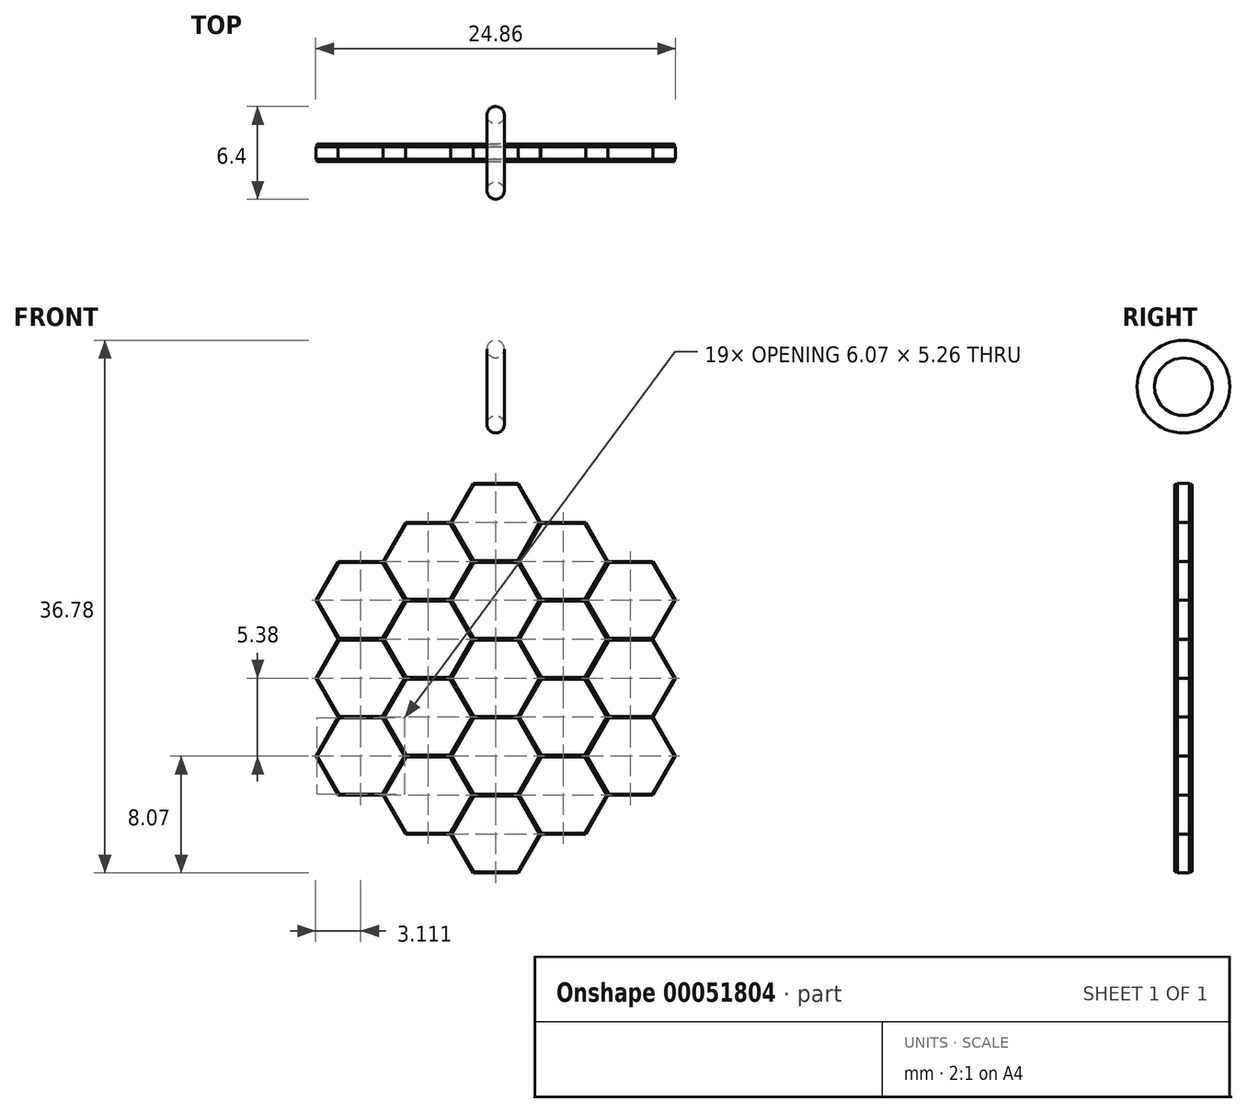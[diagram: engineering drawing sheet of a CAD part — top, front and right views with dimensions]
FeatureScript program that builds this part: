
annotation { "Feature Type Name" : "Feature", "Feature Type Description" : "" }
export const myFeature = defineFeature(function(context is Context, id is Id, definition is map)
    precondition{}
    {
        {
            var Q0;
            Q0=qCreatedBy(makeId("Front.planeOp"),FACE);
            var sketch = newSketch(context, id + "F0", { "sketchPlane" : qUnion([Q0])});
            skCircle(sketch, "E0.cCircle", {"center": v(0, 0) * mm, "radius": 4.38 * mm, "construction": true});
            skLineSegment(sketch, "E0.0", {"start": v(2.19, 3.79) * mm, "end": v(4.38, 0) * mm});
            skLineSegment(sketch, "E0.1", {"start": v(4.38, 0) * mm, "end": v(2.19, -3.79) * mm});
            skLineSegment(sketch, "E0.2", {"start": v(2.19, -3.79) * mm, "end": v(-2.19, -3.79) * mm});
            skLineSegment(sketch, "E0.3", {"start": v(-2.19, -3.79) * mm, "end": v(-4.38, 0) * mm});
            skLineSegment(sketch, "E0.4", {"start": v(-4.38, 0) * mm, "end": v(-2.19, 3.79) * mm});
            skLineSegment(sketch, "E0.5", {"start": v(-2.19, 3.79) * mm, "end": v(2.19, 3.79) * mm});
            skLineSegment(sketch, "E1.MirrorCS", {"start": v(-4.38, 7.58) * mm, "end": v(-2.19, 3.79) * mm});
            skLineSegment(sketch, "E2.MirrorCS", {"start": v(-2.19, 11.37) * mm, "end": v(-4.38, 7.58) * mm});
            skLineSegment(sketch, "E3.MirrorCS", {"start": v(2.19, 11.37) * mm, "end": v(-2.19, 11.37) * mm});
            skLineSegment(sketch, "E4.MirrorCS", {"start": v(4.38, 7.58) * mm, "end": v(2.19, 11.37) * mm});
            skLineSegment(sketch, "E5.MirrorCS", {"start": v(2.19, 3.79) * mm, "end": v(4.38, 7.58) * mm});
            skCircle(sketch, "E6.cCircle", {"center": v(0, 0) * mm, "radius": 4.28 * mm, "construction": true});
            skLineSegment(sketch, "E6.0", {"start": v(2.14, 3.7) * mm, "end": v(4.27, 0) * mm});
            skLineSegment(sketch, "E6.1", {"start": v(4.27, 0) * mm, "end": v(2.14, -3.7) * mm});
            skLineSegment(sketch, "E6.2", {"start": v(2.14, -3.7) * mm, "end": v(-2.14, -3.7) * mm});
            skLineSegment(sketch, "E6.3", {"start": v(-2.14, -3.7) * mm, "end": v(-4.27, 0) * mm});
            skLineSegment(sketch, "E6.4", {"start": v(-4.27, 0) * mm, "end": v(-2.14, 3.7) * mm});
            skLineSegment(sketch, "E6.5", {"start": v(-2.14, 3.7) * mm, "end": v(2.14, 3.7) * mm});
            skLineSegment(sketch, "E7.MirrorCS", {"start": v(-2.14, 3.88) * mm, "end": v(2.14, 3.88) * mm});
            skLineSegment(sketch, "E8.MirrorCS", {"start": v(-4.27, 7.58) * mm, "end": v(-2.14, 3.88) * mm});
            skLineSegment(sketch, "E9.MirrorCS", {"start": v(-2.14, 11.28) * mm, "end": v(-4.27, 7.58) * mm});
            skLineSegment(sketch, "E10.MirrorCS", {"start": v(2.14, 11.28) * mm, "end": v(-2.14, 11.28) * mm});
            skLineSegment(sketch, "E11.MirrorCS", {"start": v(4.27, 7.58) * mm, "end": v(2.14, 11.28) * mm});
            skLineSegment(sketch, "E12.MirrorCS", {"start": v(2.14, 3.88) * mm, "end": v(4.27, 7.58) * mm});
            skLineSegment(sketch, "E13.MirrorCS", {"start": v(2.29, 3.79) * mm, "end": v(4.43, 0.09) * mm});
            skLineSegment(sketch, "E14.MirrorCS", {"start": v(4.43, 7.5) * mm, "end": v(2.29, 3.79) * mm});
            skLineSegment(sketch, "E15.MirrorCS", {"start": v(8.7, 7.5) * mm, "end": v(4.42, 7.5) * mm});
            skLineSegment(sketch, "E16.MirrorCS", {"start": v(8.75, 7.58) * mm, "end": v(4.38, 7.58) * mm});
            skLineSegment(sketch, "E17.MirrorCS", {"start": v(10.84, 3.79) * mm, "end": v(8.7, 7.5) * mm});
            skLineSegment(sketch, "E18.MirrorCS", {"start": v(10.94, 3.79) * mm, "end": v(8.75, 7.58) * mm});
            skLineSegment(sketch, "E19.MirrorCS", {"start": v(8.7, 0.09) * mm, "end": v(10.84, 3.79) * mm});
            skLineSegment(sketch, "E20.MirrorCS", {"start": v(8.75, 0) * mm, "end": v(10.94, 3.79) * mm});
            skLineSegment(sketch, "E21.MirrorCS", {"start": v(4.43, 0.09) * mm, "end": v(8.7, 0.09) * mm});
            skLineSegment(sketch, "E22.MirrorCS", {"start": v(4.38, 0) * mm, "end": v(8.75, 0) * mm});
            skLineSegment(sketch, "E23.MirrorCS", {"start": v(4.43, -0.09) * mm, "end": v(2.29, -3.79) * mm});
            skLineSegment(sketch, "E24.MirrorCS", {"start": v(8.7, -0.09) * mm, "end": v(4.43, -0.09) * mm});
            skLineSegment(sketch, "E25.MirrorCS", {"start": v(10.84, -3.79) * mm, "end": v(8.7, -0.09) * mm});
            skLineSegment(sketch, "E26.MirrorCS", {"start": v(10.94, -3.79) * mm, "end": v(8.75, 0) * mm});
            skLineSegment(sketch, "E27.MirrorCS", {"start": v(8.7, -7.5) * mm, "end": v(10.84, -3.79) * mm});
            skLineSegment(sketch, "E28.MirrorCS", {"start": v(8.75, -7.58) * mm, "end": v(10.94, -3.79) * mm});
            skLineSegment(sketch, "E29.MirrorCS", {"start": v(4.43, -7.5) * mm, "end": v(8.7, -7.5) * mm});
            skLineSegment(sketch, "E30.MirrorCS", {"start": v(4.38, -7.58) * mm, "end": v(8.75, -7.58) * mm});
            skLineSegment(sketch, "E31.MirrorCS", {"start": v(2.29, -3.79) * mm, "end": v(4.43, -7.5) * mm});
            skLineSegment(sketch, "E32.MirrorCS", {"start": v(2.19, -3.79) * mm, "end": v(4.38, -7.58) * mm});
            skLineSegment(sketch, "E33.MirrorCS", {"start": v(2.14, -3.88) * mm, "end": v(-2.14, -3.88) * mm});
            skLineSegment(sketch, "E34.MirrorCS", {"start": v(4.27, -7.58) * mm, "end": v(2.14, -3.88) * mm});
            skLineSegment(sketch, "E35.MirrorCS", {"start": v(2.14, -11.28) * mm, "end": v(4.27, -7.58) * mm});
            skLineSegment(sketch, "E36.MirrorCS", {"start": v(2.19, -11.37) * mm, "end": v(4.38, -7.58) * mm});
            skLineSegment(sketch, "E37.MirrorCS", {"start": v(-2.14, -11.28) * mm, "end": v(2.14, -11.28) * mm});
            skLineSegment(sketch, "E38.MirrorCS", {"start": v(-2.19, -11.37) * mm, "end": v(2.19, -11.37) * mm});
            skLineSegment(sketch, "E39.MirrorCS", {"start": v(-4.27, -7.58) * mm, "end": v(-2.14, -11.28) * mm});
            skLineSegment(sketch, "E40.MirrorCS", {"start": v(-4.38, -7.58) * mm, "end": v(-2.19, -11.37) * mm});
            skLineSegment(sketch, "E41.MirrorCS", {"start": v(-2.14, -3.88) * mm, "end": v(-4.27, -7.58) * mm});
            skLineSegment(sketch, "E42.MirrorCS", {"start": v(-2.19, -3.79) * mm, "end": v(-4.38, -7.58) * mm});
            skLineSegment(sketch, "E43.MirrorCS", {"start": v(-2.29, -3.79) * mm, "end": v(-4.43, -0.09) * mm});
            skLineSegment(sketch, "E44.MirrorCS", {"start": v(-4.43, -0.09) * mm, "end": v(-8.7, -0.09) * mm});
            skLineSegment(sketch, "E45.MirrorCS", {"start": v(-4.38, 0) * mm, "end": v(-8.75, 0) * mm});
            skLineSegment(sketch, "E46.MirrorCS", {"start": v(-8.7, -0.09) * mm, "end": v(-10.84, -3.79) * mm});
            skLineSegment(sketch, "E47.MirrorCS", {"start": v(-8.75, 0) * mm, "end": v(-10.94, -3.79) * mm});
            skLineSegment(sketch, "E48.MirrorCS", {"start": v(-10.84, -3.79) * mm, "end": v(-8.7, -7.5) * mm});
            skLineSegment(sketch, "E49.MirrorCS", {"start": v(-10.94, -3.79) * mm, "end": v(-8.75, -7.58) * mm});
            skLineSegment(sketch, "E50.MirrorCS", {"start": v(-8.7, -7.5) * mm, "end": v(-4.42, -7.5) * mm});
            skLineSegment(sketch, "E51.MirrorCS", {"start": v(-8.75, -7.58) * mm, "end": v(-4.38, -7.58) * mm});
            skLineSegment(sketch, "E52.MirrorCS", {"start": v(-4.42, -7.5) * mm, "end": v(-2.29, -3.79) * mm});
            skLineSegment(sketch, "E53.MirrorCS", {"start": v(-4.42, 0.09) * mm, "end": v(-2.29, 3.79) * mm});
            skLineSegment(sketch, "E54.MirrorCS", {"start": v(-2.29, 3.79) * mm, "end": v(-4.43, 7.5) * mm});
            skLineSegment(sketch, "E55.MirrorCS", {"start": v(-4.42, 7.5) * mm, "end": v(-8.7, 7.5) * mm});
            skLineSegment(sketch, "E56.MirrorCS", {"start": v(-8.7, 7.5) * mm, "end": v(-10.84, 3.79) * mm});
            skLineSegment(sketch, "E57.MirrorCS", {"start": v(-10.84, 3.79) * mm, "end": v(-8.7, 0.09) * mm});
            skLineSegment(sketch, "E58.MirrorCS", {"start": v(-8.7, 0.09) * mm, "end": v(-4.42, 0.09) * mm});
            skLineSegment(sketch, "E59.MirrorCS", {"start": v(-8.75, 7.58) * mm, "end": v(-10.94, 3.79) * mm});
            skLineSegment(sketch, "E60.MirrorCS", {"start": v(-4.38, 7.58) * mm, "end": v(-8.75, 7.58) * mm});
            skLineSegment(sketch, "E61.MirrorCS", {"start": v(-10.94, 3.79) * mm, "end": v(-8.75, 0) * mm});
            skLineSegment(sketch, "E62.MirrorCS", {"start": v(10.99, 3.88) * mm, "end": v(8.85, 7.58) * mm});
            skLineSegment(sketch, "E63.MirrorCS", {"start": v(8.75, 7.58) * mm, "end": v(10.94, 11.37) * mm});
            skLineSegment(sketch, "E64.MirrorCS", {"start": v(8.85, 7.58) * mm, "end": v(10.99, 11.28) * mm});
            skLineSegment(sketch, "E65.MirrorCS", {"start": v(10.99, 11.28) * mm, "end": v(15.26, 11.28) * mm});
            skLineSegment(sketch, "E66.MirrorCS", {"start": v(15.31, 11.37) * mm, "end": v(10.94, 11.37) * mm});
            skLineSegment(sketch, "E67.MirrorCS", {"start": v(15.26, 11.28) * mm, "end": v(17.4, 7.58) * mm});
            skLineSegment(sketch, "E68.MirrorCS", {"start": v(15.31, 11.37) * mm, "end": v(17.5, 7.58) * mm});
            skLineSegment(sketch, "E69.MirrorCS", {"start": v(17.4, 7.58) * mm, "end": v(15.26, 3.88) * mm});
            skLineSegment(sketch, "E70.MirrorCS", {"start": v(17.5, 7.58) * mm, "end": v(15.31, 3.79) * mm});
            skLineSegment(sketch, "E71.MirrorCS", {"start": v(15.26, 3.88) * mm, "end": v(10.99, 3.88) * mm});
            skLineSegment(sketch, "E72.MirrorCS", {"start": v(15.31, 3.79) * mm, "end": v(10.94, 3.79) * mm});
            skLineSegment(sketch, "E73.MirrorCS", {"start": v(8.85, 0) * mm, "end": v(10.99, 3.7) * mm});
            skLineSegment(sketch, "E74.MirrorCS", {"start": v(10.99, 3.7) * mm, "end": v(15.26, 3.7) * mm});
            skLineSegment(sketch, "E75.MirrorCS", {"start": v(15.26, 3.7) * mm, "end": v(17.4, 0) * mm});
            skLineSegment(sketch, "E76.MirrorCS", {"start": v(17.4, 0) * mm, "end": v(15.26, -3.7) * mm});
            skLineSegment(sketch, "E77.MirrorCS", {"start": v(15.26, -3.7) * mm, "end": v(10.99, -3.7) * mm});
            skLineSegment(sketch, "E78.MirrorCS", {"start": v(10.99, -3.7) * mm, "end": v(8.85, 0) * mm});
            skLineSegment(sketch, "E79.MirrorCS", {"start": v(15.31, 3.79) * mm, "end": v(17.5, 0) * mm});
            skLineSegment(sketch, "E80.MirrorCS", {"start": v(15.31, -3.79) * mm, "end": v(17.5, 0) * mm});
            skLineSegment(sketch, "E81.MirrorCS", {"start": v(15.31, -3.79) * mm, "end": v(10.94, -3.79) * mm});
            skLineSegment(sketch, "E82.MirrorCS", {"start": v(2.14, 11.45) * mm, "end": v(-2.14, 11.45) * mm});
            skLineSegment(sketch, "E83.MirrorCS", {"start": v(-2.14, 11.45) * mm, "end": v(-4.27, 15.16) * mm});
            skLineSegment(sketch, "E84.MirrorCS", {"start": v(-2.19, 11.37) * mm, "end": v(-4.38, 15.16) * mm});
            skLineSegment(sketch, "E85.MirrorCS", {"start": v(-4.27, 15.16) * mm, "end": v(-2.14, 18.86) * mm});
            skLineSegment(sketch, "E86.MirrorCS", {"start": v(-4.38, 15.16) * mm, "end": v(-2.19, 18.94) * mm});
            skLineSegment(sketch, "E87.MirrorCS", {"start": v(-2.14, 18.86) * mm, "end": v(2.14, 18.86) * mm});
            skLineSegment(sketch, "E88.MirrorCS", {"start": v(-2.19, 18.94) * mm, "end": v(2.19, 18.94) * mm});
            skLineSegment(sketch, "E89.MirrorCS", {"start": v(2.14, 18.86) * mm, "end": v(4.27, 15.16) * mm});
            skLineSegment(sketch, "E90.MirrorCS", {"start": v(2.19, 18.94) * mm, "end": v(4.37, 15.16) * mm});
            skLineSegment(sketch, "E91.MirrorCS", {"start": v(4.27, 15.16) * mm, "end": v(2.14, 11.45) * mm});
            skLineSegment(sketch, "E92.MirrorCS", {"start": v(4.37, 15.16) * mm, "end": v(2.19, 11.37) * mm});
            skLineSegment(sketch, "E93.MirrorCS", {"start": v(-2.14, -11.45) * mm, "end": v(2.14, -11.45) * mm});
            skLineSegment(sketch, "E94.MirrorCS", {"start": v(-4.27, -15.16) * mm, "end": v(-2.14, -11.45) * mm});
            skLineSegment(sketch, "E95.MirrorCS", {"start": v(-4.37, -15.16) * mm, "end": v(-2.19, -11.37) * mm});
            skLineSegment(sketch, "E96.MirrorCS", {"start": v(-2.14, -18.86) * mm, "end": v(-4.27, -15.16) * mm});
            skLineSegment(sketch, "E97.MirrorCS", {"start": v(-2.19, -18.94) * mm, "end": v(-4.38, -15.16) * mm});
            skLineSegment(sketch, "E98.MirrorCS", {"start": v(2.14, -18.86) * mm, "end": v(-2.14, -18.86) * mm});
            skLineSegment(sketch, "E99.MirrorCS", {"start": v(2.19, -18.94) * mm, "end": v(-2.19, -18.94) * mm});
            skLineSegment(sketch, "E100.MirrorCS", {"start": v(4.27, -15.16) * mm, "end": v(2.14, -18.86) * mm});
            skLineSegment(sketch, "E101.MirrorCS", {"start": v(2.19, -18.94) * mm, "end": v(4.38, -15.16) * mm});
            skLineSegment(sketch, "E102.MirrorCS", {"start": v(2.14, -11.45) * mm, "end": v(4.27, -15.16) * mm});
            skLineSegment(sketch, "E103.MirrorCS", {"start": v(2.19, -11.37) * mm, "end": v(4.38, -15.16) * mm});
            skLineSegment(sketch, "E104.MirrorCS", {"start": v(8.7, 7.66) * mm, "end": v(4.42, 7.66) * mm});
            skLineSegment(sketch, "E105.MirrorCS", {"start": v(4.43, 7.66) * mm, "end": v(2.29, 11.37) * mm});
            skLineSegment(sketch, "E106.MirrorCS", {"start": v(2.29, 11.37) * mm, "end": v(4.42, 15.07) * mm});
            skLineSegment(sketch, "E107.MirrorCS", {"start": v(4.42, 15.07) * mm, "end": v(8.7, 15.07) * mm});
            skLineSegment(sketch, "E108.MirrorCS", {"start": v(8.7, 15.07) * mm, "end": v(10.84, 11.37) * mm});
            skLineSegment(sketch, "E109.MirrorCS", {"start": v(10.84, 11.37) * mm, "end": v(8.7, 7.66) * mm});
            skLineSegment(sketch, "E110.MirrorCS", {"start": v(8.75, 15.16) * mm, "end": v(10.94, 11.37) * mm});
            skLineSegment(sketch, "E111.MirrorCS", {"start": v(4.37, 15.16) * mm, "end": v(8.75, 15.16) * mm});
            skLineSegment(sketch, "E112.MirrorCS", {"start": v(4.43, -7.66) * mm, "end": v(8.7, -7.66) * mm});
            skLineSegment(sketch, "E113.MirrorCS", {"start": v(2.29, -11.37) * mm, "end": v(4.43, -7.66) * mm});
            skLineSegment(sketch, "E114.MirrorCS", {"start": v(4.43, -15.07) * mm, "end": v(2.29, -11.37) * mm});
            skLineSegment(sketch, "E115.MirrorCS", {"start": v(8.7, -15.07) * mm, "end": v(4.43, -15.07) * mm});
            skLineSegment(sketch, "E116.MirrorCS", {"start": v(4.38, -15.16) * mm, "end": v(8.75, -15.16) * mm});
            skLineSegment(sketch, "E117.MirrorCS", {"start": v(10.84, -11.37) * mm, "end": v(8.7, -15.07) * mm});
            skLineSegment(sketch, "E118.MirrorCS", {"start": v(10.94, -11.37) * mm, "end": v(8.75, -15.16) * mm});
            skLineSegment(sketch, "E119.MirrorCS", {"start": v(8.7, -7.66) * mm, "end": v(10.84, -11.37) * mm});
            skLineSegment(sketch, "E120.MirrorCS", {"start": v(8.75, -7.58) * mm, "end": v(10.94, -11.37) * mm});
            skLineSegment(sketch, "E121.MirrorCS", {"start": v(8.85, -7.58) * mm, "end": v(10.99, -3.88) * mm});
            skLineSegment(sketch, "E122.MirrorCS", {"start": v(10.99, -11.28) * mm, "end": v(8.85, -7.58) * mm});
            skLineSegment(sketch, "E123.MirrorCS", {"start": v(15.26, -11.28) * mm, "end": v(10.99, -11.28) * mm});
            skLineSegment(sketch, "E124.MirrorCS", {"start": v(15.31, -11.37) * mm, "end": v(10.94, -11.37) * mm});
            skLineSegment(sketch, "E125.MirrorCS", {"start": v(17.4, -7.58) * mm, "end": v(15.26, -11.28) * mm});
            skLineSegment(sketch, "E126.MirrorCS", {"start": v(17.5, -7.58) * mm, "end": v(15.31, -11.37) * mm});
            skLineSegment(sketch, "E127.MirrorCS", {"start": v(15.26, -3.88) * mm, "end": v(17.4, -7.58) * mm});
            skLineSegment(sketch, "E128.MirrorCS", {"start": v(17.5, -7.58) * mm, "end": v(15.31, -3.79) * mm});
            skLineSegment(sketch, "E129.MirrorCS", {"start": v(10.99, -3.88) * mm, "end": v(15.26, -3.88) * mm});
            skLineSegment(sketch, "E130.MirrorCS", {"start": v(-4.42, 7.66) * mm, "end": v(-8.7, 7.66) * mm});
            skLineSegment(sketch, "E131.MirrorCS", {"start": v(-2.29, 11.37) * mm, "end": v(-4.42, 7.66) * mm});
            skLineSegment(sketch, "E132.MirrorCS", {"start": v(-4.43, 15.07) * mm, "end": v(-2.29, 11.37) * mm});
            skLineSegment(sketch, "E133.MirrorCS", {"start": v(-8.7, 15.07) * mm, "end": v(-4.42, 15.07) * mm});
            skLineSegment(sketch, "E134.MirrorCS", {"start": v(-10.84, 11.37) * mm, "end": v(-8.7, 15.07) * mm});
            skLineSegment(sketch, "E135.MirrorCS", {"start": v(-8.7, 7.66) * mm, "end": v(-10.84, 11.37) * mm});
            skLineSegment(sketch, "E136.MirrorCS", {"start": v(-8.75, 7.58) * mm, "end": v(-10.94, 11.37) * mm});
            skLineSegment(sketch, "E137.MirrorCS", {"start": v(-10.94, 11.37) * mm, "end": v(-8.75, 15.16) * mm});
            skLineSegment(sketch, "E138.MirrorCS", {"start": v(-4.38, 15.16) * mm, "end": v(-8.75, 15.16) * mm});
            skLineSegment(sketch, "E139.MirrorCS", {"start": v(-8.7, -7.66) * mm, "end": v(-4.42, -7.66) * mm});
            skLineSegment(sketch, "E140.MirrorCS", {"start": v(-4.42, -7.66) * mm, "end": v(-2.29, -11.37) * mm});
            skLineSegment(sketch, "E141.MirrorCS", {"start": v(-2.29, -11.37) * mm, "end": v(-4.42, -15.07) * mm});
            skLineSegment(sketch, "E142.MirrorCS", {"start": v(-4.42, -15.07) * mm, "end": v(-8.7, -15.07) * mm});
            skLineSegment(sketch, "E143.MirrorCS", {"start": v(-4.37, -15.16) * mm, "end": v(-8.75, -15.16) * mm});
            skLineSegment(sketch, "E144.MirrorCS", {"start": v(-8.7, -15.07) * mm, "end": v(-10.84, -11.37) * mm});
            skLineSegment(sketch, "E145.MirrorCS", {"start": v(-8.75, -15.16) * mm, "end": v(-10.94, -11.37) * mm});
            skLineSegment(sketch, "E146.MirrorCS", {"start": v(-10.84, -11.37) * mm, "end": v(-8.7, -7.66) * mm});
            skLineSegment(sketch, "E147.MirrorCS", {"start": v(-10.94, -11.37) * mm, "end": v(-8.75, -7.58) * mm});
            skLineSegment(sketch, "E148.MirrorCS", {"start": v(-8.85, 7.58) * mm, "end": v(-10.99, 11.28) * mm});
            skLineSegment(sketch, "E149.MirrorCS", {"start": v(-10.99, 11.28) * mm, "end": v(-15.26, 11.28) * mm});
            skLineSegment(sketch, "E150.MirrorCS", {"start": v(-15.26, 11.28) * mm, "end": v(-17.4, 7.58) * mm});
            skLineSegment(sketch, "E151.MirrorCS", {"start": v(-17.4, 7.58) * mm, "end": v(-15.26, 3.88) * mm});
            skLineSegment(sketch, "E152.MirrorCS", {"start": v(-15.26, 3.88) * mm, "end": v(-10.99, 3.88) * mm});
            skLineSegment(sketch, "E153.MirrorCS", {"start": v(-10.99, 3.88) * mm, "end": v(-8.85, 7.58) * mm});
            skLineSegment(sketch, "E154.MirrorCS", {"start": v(-10.94, 11.37) * mm, "end": v(-15.31, 11.37) * mm});
            skLineSegment(sketch, "E155.MirrorCS", {"start": v(-17.5, 7.58) * mm, "end": v(-15.31, 11.37) * mm});
            skLineSegment(sketch, "E156.MirrorCS", {"start": v(-15.31, 3.79) * mm, "end": v(-17.5, 7.58) * mm});
            skLineSegment(sketch, "E157.MirrorCS", {"start": v(-15.31, 3.79) * mm, "end": v(-10.94, 3.79) * mm});
            skLineSegment(sketch, "E158.MirrorCS", {"start": v(-15.26, 3.7) * mm, "end": v(-10.99, 3.7) * mm});
            skLineSegment(sketch, "E159.MirrorCS", {"start": v(-17.4, 0) * mm, "end": v(-15.26, 3.7) * mm});
            skLineSegment(sketch, "E160.MirrorCS", {"start": v(-15.26, -3.7) * mm, "end": v(-17.4, 0) * mm});
            skLineSegment(sketch, "E161.MirrorCS", {"start": v(-15.31, 3.79) * mm, "end": v(-17.5, 0) * mm});
            skLineSegment(sketch, "E162.MirrorCS", {"start": v(-17.5, 0) * mm, "end": v(-15.31, -3.79) * mm});
            skLineSegment(sketch, "E163.MirrorCS", {"start": v(-10.99, -3.7) * mm, "end": v(-15.26, -3.7) * mm});
            skLineSegment(sketch, "E164.MirrorCS", {"start": v(-10.94, -3.79) * mm, "end": v(-15.31, -3.79) * mm});
            skLineSegment(sketch, "E165.MirrorCS", {"start": v(-8.85, 0) * mm, "end": v(-10.99, -3.7) * mm});
            skLineSegment(sketch, "E166.MirrorCS", {"start": v(-10.99, 3.7) * mm, "end": v(-8.85, 0) * mm});
            skLineSegment(sketch, "E167.MirrorCS", {"start": v(-10.99, -3.88) * mm, "end": v(-15.26, -3.88) * mm});
            skLineSegment(sketch, "E168.MirrorCS", {"start": v(-15.26, -3.88) * mm, "end": v(-17.4, -7.58) * mm});
            skLineSegment(sketch, "E169.MirrorCS", {"start": v(-17.5, -7.58) * mm, "end": v(-15.31, -3.79) * mm});
            skLineSegment(sketch, "E170.MirrorCS", {"start": v(-17.4, -7.58) * mm, "end": v(-15.26, -11.28) * mm});
            skLineSegment(sketch, "E171.MirrorCS", {"start": v(-15.31, -11.37) * mm, "end": v(-17.5, -7.58) * mm});
            skLineSegment(sketch, "E172.MirrorCS", {"start": v(-15.26, -11.28) * mm, "end": v(-10.99, -11.28) * mm});
            skLineSegment(sketch, "E173.MirrorCS", {"start": v(-15.31, -11.37) * mm, "end": v(-10.94, -11.37) * mm});
            skLineSegment(sketch, "E174.MirrorCS", {"start": v(-10.99, -11.28) * mm, "end": v(-8.85, -7.58) * mm});
            skLineSegment(sketch, "E175.MirrorCS", {"start": v(-8.85, -7.58) * mm, "end": v(-10.99, -3.88) * mm});
            skSolve(sketch);
        }
        {
            var Q0;
            Q0=makeQuery(id+"F0.imprint","IMPRINT",FACE,{"disambiguationData":[TD([[makeQuery(id+"F0.imprint","IMPRINT",EDGE,{"derivedFrom":sQuery(id+"F0.wireOp",EDGE,"E0.3")}),1.0]])]});
            var Q1;
            Q1=makeQuery(id+"F0.imprint","IMPRINT",FACE,{"disambiguationData":[TD([[makeQuery(id+"F0.imprint","IMPRINT",EDGE,{"derivedFrom":sQuery(id+"F0.wireOp",EDGE,"E47.MirrorCS")}),-1.0]])]});
            var Q2;
            Q2=makeQuery(id+"F0.imprint","IMPRINT",FACE,{"disambiguationData":[TD([[makeQuery(id+"F0.imprint","IMPRINT",EDGE,{"derivedFrom":sQuery(id+"F0.wireOp",EDGE,"E49.MirrorCS")}),-1.0]])]});
            var Q3;
            Q3=makeQuery(id+"F0.imprint","IMPRINT",FACE,{"disambiguationData":[TD([[makeQuery(id+"F0.imprint","IMPRINT",EDGE,{"derivedFrom":sQuery(id+"F0.wireOp",EDGE,"E0.4")}),1.0]])]});
            var Q4;
            Q4=makeQuery(id+"F0.imprint","IMPRINT",FACE,{"disambiguationData":[TD([[makeQuery(id+"F0.imprint","IMPRINT",EDGE,{"derivedFrom":sQuery(id+"F0.wireOp",EDGE,"E59.MirrorCS")}),-1.0]])]});
            var Q5;
            Q5=makeQuery(id+"F0.imprint","IMPRINT",FACE,{"disambiguationData":[TD([[makeQuery(id+"F0.imprint","IMPRINT",EDGE,{"derivedFrom":sQuery(id+"F0.wireOp",EDGE,"E0.0")}),-1.0]])]});
            var Q6;
            Q6=makeQuery(id+"F0.imprint","IMPRINT",FACE,{"disambiguationData":[TD([[makeQuery(id+"F0.imprint","IMPRINT",EDGE,{"derivedFrom":sQuery(id+"F0.wireOp",EDGE,"E0.2")}),1.0]])]});
            var Q7;
            Q7=makeQuery(id+"F0.imprint","IMPRINT",FACE,{"disambiguationData":[TD([[makeQuery(id+"F0.imprint","IMPRINT",EDGE,{"derivedFrom":sQuery(id+"F0.wireOp",EDGE,"E40.MirrorCS")}),-1.0]])]});
            var Q8;
            Q8=makeQuery(id+"F0.imprint","IMPRINT",FACE,{"disambiguationData":[TD([[makeQuery(id+"F0.imprint","IMPRINT",EDGE,{"derivedFrom":sQuery(id+"F0.wireOp",EDGE,"E38.MirrorCS")}),-1.0]])]});
            var Q9;
            Q9=makeQuery(id+"F0.imprint","IMPRINT",FACE,{"disambiguationData":[TD([[makeQuery(id+"F0.imprint","IMPRINT",EDGE,{"derivedFrom":sQuery(id+"F0.wireOp",EDGE,"E30.MirrorCS")}),-1.0]])]});
            var Q10;
            Q10=makeQuery(id+"F0.imprint","IMPRINT",FACE,{"disambiguationData":[TD([[makeQuery(id+"F0.imprint","IMPRINT",EDGE,{"derivedFrom":sQuery(id+"F0.wireOp",EDGE,"E0.1")}),1.0]])]});
            var Q11;
            Q11=makeQuery(id+"F0.imprint","IMPRINT",FACE,{"disambiguationData":[TD([[makeQuery(id+"F0.imprint","IMPRINT",EDGE,{"derivedFrom":sQuery(id+"F0.wireOp",EDGE,"E0.0")}),1.0]])]});
            var Q12;
            Q12=makeQuery(id+"F0.imprint","IMPRINT",FACE,{"disambiguationData":[TD([[makeQuery(id+"F0.imprint","IMPRINT",EDGE,{"derivedFrom":sQuery(id+"F0.wireOp",EDGE,"E0.5")}),1.0]])]});
            var Q13;
            Q13=makeQuery(id+"F0.imprint","IMPRINT",FACE,{"disambiguationData":[TD([[makeQuery(id+"F0.imprint","IMPRINT",EDGE,{"derivedFrom":sQuery(id+"F0.wireOp",EDGE,"E2.MirrorCS")}),-1.0]])]});
            var Q14;
            Q14=makeQuery(id+"F0.imprint","IMPRINT",FACE,{"disambiguationData":[TD([[makeQuery(id+"F0.imprint","IMPRINT",EDGE,{"derivedFrom":sQuery(id+"F0.wireOp",EDGE,"E3.MirrorCS")}),-1.0]])]});
            var Q15;
            Q15=makeQuery(id+"F0.imprint","IMPRINT",FACE,{"disambiguationData":[TD([[makeQuery(id+"F0.imprint","IMPRINT",EDGE,{"derivedFrom":sQuery(id+"F0.wireOp",EDGE,"E4.MirrorCS")}),-1.0]])]});
            var Q16;
            Q16=makeQuery(id+"F0.imprint","IMPRINT",FACE,{"disambiguationData":[TD([[makeQuery(id+"F0.imprint","IMPRINT",EDGE,{"derivedFrom":sQuery(id+"F0.wireOp",EDGE,"E18.MirrorCS")}),-1.0]])]});
            var Q17;
            Q17=makeQuery(id+"F0.imprint","IMPRINT",FACE,{"disambiguationData":[TD([[makeQuery(id+"F0.imprint","IMPRINT",EDGE,{"derivedFrom":sQuery(id+"F0.wireOp",EDGE,"E20.MirrorCS")}),-1.0]])]});
            var Q18;
            Q18=makeQuery(id+"F0.imprint","IMPRINT",FACE,{"disambiguationData":[TD([[makeQuery(id+"F0.imprint","IMPRINT",EDGE,{"derivedFrom":sQuery(id+"F0.wireOp",EDGE,"E28.MirrorCS")}),-1.0]])]});
            extrude(context, id + "F1", {"entities" : qUnion([Q0, Q1, Q2, Q3, Q4, Q5, Q6, Q7, Q8, Q9, Q10, Q11, Q12, Q13, Q14, Q15, Q16, Q17, Q18]), "endBound" : BoundingType.SYMMETRIC, "offsetDistance" : 25 * mm, "depth" : 1.2 * mm});
        }
        {
            var Q0;
            Q0=makeQuery(id+"F0.imprint","IMPRINT",FACE,{"disambiguationData":[TD([[makeQuery(id+"F0.imprint","IMPRINT",EDGE,{"derivedFrom":sQuery(id+"F0.wireOp",EDGE,"E167.MirrorCS")}),1.0]])]});
            var Q1;
            Q1=makeQuery(id+"F0.imprint","IMPRINT",FACE,{"disambiguationData":[TD([[makeQuery(id+"F0.imprint","IMPRINT",EDGE,{"derivedFrom":sQuery(id+"F0.wireOp",EDGE,"E158.MirrorCS")}),-1.0]])]});
            var Q2;
            Q2=makeQuery(id+"F0.imprint","IMPRINT",FACE,{"disambiguationData":[TD([[makeQuery(id+"F0.imprint","IMPRINT",EDGE,{"derivedFrom":sQuery(id+"F0.wireOp",EDGE,"E148.MirrorCS")}),1.0]])]});
            var Q3;
            Q3=makeQuery(id+"F0.imprint","IMPRINT",FACE,{"disambiguationData":[TD([[makeQuery(id+"F0.imprint","IMPRINT",EDGE,{"derivedFrom":sQuery(id+"F0.wireOp",EDGE,"E139.MirrorCS")}),-1.0]])]});
            var Q4;
            Q4=makeQuery(id+"F0.imprint","IMPRINT",FACE,{"disambiguationData":[TD([[makeQuery(id+"F0.imprint","IMPRINT",EDGE,{"derivedFrom":sQuery(id+"F0.wireOp",EDGE,"E43.MirrorCS")}),1.0]])]});
            var Q5;
            Q5=makeQuery(id+"F0.imprint","IMPRINT",FACE,{"disambiguationData":[TD([[makeQuery(id+"F0.imprint","IMPRINT",EDGE,{"derivedFrom":sQuery(id+"F0.wireOp",EDGE,"E53.MirrorCS")}),1.0]])]});
            var Q6;
            Q6=makeQuery(id+"F0.imprint","IMPRINT",FACE,{"disambiguationData":[TD([[makeQuery(id+"F0.imprint","IMPRINT",EDGE,{"derivedFrom":sQuery(id+"F0.wireOp",EDGE,"E130.MirrorCS")}),-1.0]])]});
            var Q7;
            Q7=makeQuery(id+"F0.imprint","IMPRINT",FACE,{"disambiguationData":[TD([[makeQuery(id+"F0.imprint","IMPRINT",EDGE,{"derivedFrom":sQuery(id+"F0.wireOp",EDGE,"E93.MirrorCS")}),-1.0]])]});
            var Q8;
            Q8=makeQuery(id+"F0.imprint","IMPRINT",FACE,{"disambiguationData":[TD([[makeQuery(id+"F0.imprint","IMPRINT",EDGE,{"derivedFrom":sQuery(id+"F0.wireOp",EDGE,"E33.MirrorCS")}),1.0]])]});
            var Q9;
            Q9=makeQuery(id+"F0.imprint","IMPRINT",FACE,{"disambiguationData":[TD([[makeQuery(id+"F0.imprint","IMPRINT",EDGE,{"derivedFrom":sQuery(id+"F0.wireOp",EDGE,"E7.MirrorCS")}),1.0]])]});
            var Q10;
            Q10=makeQuery(id+"F0.imprint","IMPRINT",FACE,{"disambiguationData":[TD([[makeQuery(id+"F0.imprint","IMPRINT",EDGE,{"derivedFrom":sQuery(id+"F0.wireOp",EDGE,"E82.MirrorCS")}),-1.0]])]});
            var Q11;
            Q11=makeQuery(id+"F0.imprint","IMPRINT",FACE,{"disambiguationData":[TD([[makeQuery(id+"F0.imprint","IMPRINT",EDGE,{"derivedFrom":sQuery(id+"F0.wireOp",EDGE,"E112.MirrorCS")}),-1.0]])]});
            var Q12;
            Q12=makeQuery(id+"F0.imprint","IMPRINT",FACE,{"disambiguationData":[TD([[makeQuery(id+"F0.imprint","IMPRINT",EDGE,{"derivedFrom":sQuery(id+"F0.wireOp",EDGE,"E23.MirrorCS")}),1.0]])]});
            var Q13;
            Q13=makeQuery(id+"F0.imprint","IMPRINT",FACE,{"disambiguationData":[TD([[makeQuery(id+"F0.imprint","IMPRINT",EDGE,{"derivedFrom":sQuery(id+"F0.wireOp",EDGE,"E13.MirrorCS")}),1.0]])]});
            var Q14;
            Q14=makeQuery(id+"F0.imprint","IMPRINT",FACE,{"disambiguationData":[TD([[makeQuery(id+"F0.imprint","IMPRINT",EDGE,{"derivedFrom":sQuery(id+"F0.wireOp",EDGE,"E104.MirrorCS")}),-1.0]])]});
            var Q15;
            Q15=makeQuery(id+"F0.imprint","IMPRINT",FACE,{"disambiguationData":[TD([[makeQuery(id+"F0.imprint","IMPRINT",EDGE,{"derivedFrom":sQuery(id+"F0.wireOp",EDGE,"E121.MirrorCS")}),-1.0]])]});
            var Q16;
            Q16=makeQuery(id+"F0.imprint","IMPRINT",FACE,{"disambiguationData":[TD([[makeQuery(id+"F0.imprint","IMPRINT",EDGE,{"derivedFrom":sQuery(id+"F0.wireOp",EDGE,"E73.MirrorCS")}),-1.0]])]});
            var Q17;
            Q17=makeQuery(id+"F0.imprint","IMPRINT",FACE,{"disambiguationData":[TD([[makeQuery(id+"F0.imprint","IMPRINT",EDGE,{"derivedFrom":sQuery(id+"F0.wireOp",EDGE,"E62.MirrorCS")}),-1.0]])]});
            extrude(context, id + "F2", {"entities" : qUnion([Q0, Q1, Q2, Q3, Q4, Q5, Q6, Q7, Q8, Q9, Q10, Q11, Q12, Q13, Q14, Q15, Q16, Q17]), "operationType" : NewBodyOperationType.ADD, "endBound" : BoundingType.SYMMETRIC, "depth" : 1.7 * mm});
        }
        {
            var Q0;
            Q0=qCreatedBy(makeId("Front.planeOp"),FACE);
            var sketch = newSketch(context, id + "F3", { "sketchPlane" : qUnion([Q0])});
            skLineSegment(sketch, "E176", {"start": v(-4.58, 22.7) * mm, "end": v(3.46, 22.7) * mm});
            skCircle(sketch, "E177", {"center": v(0, 25.3) * mm, "radius": 0.6 * mm});
            skSolve(sketch);
        }
        {
            var Q0;
            Q0 = qSketchRegion(id + "F3", true);
            var Q1;
            Q1=sQuery(id+"F3.wireOp",EDGE,"E176");
            revolve(context, id + "F4", {"entities" : qUnion([Q0]), "axis" : qUnion([Q1]), "revolveType" : RevolveType.FULL});
        }
        {
            var Q0;
            Q0=makeQuery(id+"F4.opRevolve","SWEPT_BODY",BODY,{"disambiguationData":[OSD([sQuery(id+"F3.wireOp",EDGE,"E177")])]});
            transform(context, id + "F5", {"entities" : qUnion([Q0]), "transformType" : TransformType.TRANSLATION_3D, "dx" : 0 * mm, "dy" : 0 * mm, "dz" : -2.58 * mm, "makeCopy" : false});
        }
        {
            var Q0;
            Q0=makeQuery(id+"F1.opExtrude","SWEPT_BODY",BODY,{"disambiguationData":[OSD([sQuery(id+"F0.wireOp",EDGE,"E6.0"),sQuery(id+"F0.wireOp",EDGE,"E6.1"),sQuery(id+"F0.wireOp",EDGE,"E6.2"),sQuery(id+"F0.wireOp",EDGE,"E6.3"),sQuery(id+"F0.wireOp",EDGE,"E6.4"),sQuery(id+"F0.wireOp",EDGE,"E6.5"),sQuery(id+"F0.wireOp",EDGE,"E7.MirrorCS"),sQuery(id+"F0.wireOp",EDGE,"E8.MirrorCS"),sQuery(id+"F0.wireOp",EDGE,"E9.MirrorCS"),sQuery(id+"F0.wireOp",EDGE,"E10.MirrorCS"),sQuery(id+"F0.wireOp",EDGE,"E11.MirrorCS"),sQuery(id+"F0.wireOp",EDGE,"E12.MirrorCS"),sQuery(id+"F0.wireOp",EDGE,"E13.MirrorCS"),sQuery(id+"F0.wireOp",EDGE,"E14.MirrorCS"),sQuery(id+"F0.wireOp",EDGE,"E15.MirrorCS"),sQuery(id+"F0.wireOp",EDGE,"E17.MirrorCS"),sQuery(id+"F0.wireOp",EDGE,"E19.MirrorCS"),sQuery(id+"F0.wireOp",EDGE,"E21.MirrorCS"),sQuery(id+"F0.wireOp",EDGE,"E23.MirrorCS"),sQuery(id+"F0.wireOp",EDGE,"E24.MirrorCS"),sQuery(id+"F0.wireOp",EDGE,"E25.MirrorCS"),sQuery(id+"F0.wireOp",EDGE,"E27.MirrorCS"),sQuery(id+"F0.wireOp",EDGE,"E29.MirrorCS"),sQuery(id+"F0.wireOp",EDGE,"E31.MirrorCS"),sQuery(id+"F0.wireOp",EDGE,"E33.MirrorCS"),sQuery(id+"F0.wireOp",EDGE,"E34.MirrorCS"),sQuery(id+"F0.wireOp",EDGE,"E35.MirrorCS"),sQuery(id+"F0.wireOp",EDGE,"E37.MirrorCS"),sQuery(id+"F0.wireOp",EDGE,"E39.MirrorCS"),sQuery(id+"F0.wireOp",EDGE,"E41.MirrorCS"),sQuery(id+"F0.wireOp",EDGE,"E43.MirrorCS"),sQuery(id+"F0.wireOp",EDGE,"E44.MirrorCS"),sQuery(id+"F0.wireOp",EDGE,"E46.MirrorCS"),sQuery(id+"F0.wireOp",EDGE,"E48.MirrorCS"),sQuery(id+"F0.wireOp",EDGE,"E50.MirrorCS"),sQuery(id+"F0.wireOp",EDGE,"E52.MirrorCS"),sQuery(id+"F0.wireOp",EDGE,"E53.MirrorCS"),sQuery(id+"F0.wireOp",EDGE,"E54.MirrorCS"),sQuery(id+"F0.wireOp",EDGE,"E55.MirrorCS"),sQuery(id+"F0.wireOp",EDGE,"E56.MirrorCS"),sQuery(id+"F0.wireOp",EDGE,"E57.MirrorCS"),sQuery(id+"F0.wireOp",EDGE,"E58.MirrorCS"),sQuery(id+"F0.wireOp",EDGE,"E62.MirrorCS"),sQuery(id+"F0.wireOp",EDGE,"E64.MirrorCS"),sQuery(id+"F0.wireOp",EDGE,"E65.MirrorCS"),sQuery(id+"F0.wireOp",EDGE,"E66.MirrorCS"),sQuery(id+"F0.wireOp",EDGE,"E67.MirrorCS"),sQuery(id+"F0.wireOp",EDGE,"E68.MirrorCS"),sQuery(id+"F0.wireOp",EDGE,"E69.MirrorCS"),sQuery(id+"F0.wireOp",EDGE,"E70.MirrorCS"),sQuery(id+"F0.wireOp",EDGE,"E71.MirrorCS"),sQuery(id+"F0.wireOp",EDGE,"E73.MirrorCS"),sQuery(id+"F0.wireOp",EDGE,"E74.MirrorCS"),sQuery(id+"F0.wireOp",EDGE,"E75.MirrorCS"),sQuery(id+"F0.wireOp",EDGE,"E76.MirrorCS"),sQuery(id+"F0.wireOp",EDGE,"E77.MirrorCS"),sQuery(id+"F0.wireOp",EDGE,"E78.MirrorCS"),sQuery(id+"F0.wireOp",EDGE,"E79.MirrorCS"),sQuery(id+"F0.wireOp",EDGE,"E80.MirrorCS"),sQuery(id+"F0.wireOp",EDGE,"E82.MirrorCS"),sQuery(id+"F0.wireOp",EDGE,"E83.MirrorCS"),sQuery(id+"F0.wireOp",EDGE,"E85.MirrorCS"),sQuery(id+"F0.wireOp",EDGE,"E86.MirrorCS"),sQuery(id+"F0.wireOp",EDGE,"E87.MirrorCS"),sQuery(id+"F0.wireOp",EDGE,"E88.MirrorCS"),sQuery(id+"F0.wireOp",EDGE,"E89.MirrorCS"),sQuery(id+"F0.wireOp",EDGE,"E90.MirrorCS"),sQuery(id+"F0.wireOp",EDGE,"E91.MirrorCS"),sQuery(id+"F0.wireOp",EDGE,"E93.MirrorCS"),sQuery(id+"F0.wireOp",EDGE,"E94.MirrorCS"),sQuery(id+"F0.wireOp",EDGE,"E96.MirrorCS"),sQuery(id+"F0.wireOp",EDGE,"E97.MirrorCS"),sQuery(id+"F0.wireOp",EDGE,"E98.MirrorCS"),sQuery(id+"F0.wireOp",EDGE,"E99.MirrorCS"),sQuery(id+"F0.wireOp",EDGE,"E100.MirrorCS"),sQuery(id+"F0.wireOp",EDGE,"E101.MirrorCS"),sQuery(id+"F0.wireOp",EDGE,"E102.MirrorCS"),sQuery(id+"F0.wireOp",EDGE,"E104.MirrorCS"),sQuery(id+"F0.wireOp",EDGE,"E105.MirrorCS"),sQuery(id+"F0.wireOp",EDGE,"E106.MirrorCS"),sQuery(id+"F0.wireOp",EDGE,"E107.MirrorCS"),sQuery(id+"F0.wireOp",EDGE,"E108.MirrorCS"),sQuery(id+"F0.wireOp",EDGE,"E109.MirrorCS"),sQuery(id+"F0.wireOp",EDGE,"E110.MirrorCS"),sQuery(id+"F0.wireOp",EDGE,"E111.MirrorCS"),sQuery(id+"F0.wireOp",EDGE,"E112.MirrorCS"),sQuery(id+"F0.wireOp",EDGE,"E113.MirrorCS"),sQuery(id+"F0.wireOp",EDGE,"E114.MirrorCS"),sQuery(id+"F0.wireOp",EDGE,"E115.MirrorCS"),sQuery(id+"F0.wireOp",EDGE,"E116.MirrorCS"),sQuery(id+"F0.wireOp",EDGE,"E117.MirrorCS"),sQuery(id+"F0.wireOp",EDGE,"E118.MirrorCS"),sQuery(id+"F0.wireOp",EDGE,"E119.MirrorCS"),sQuery(id+"F0.wireOp",EDGE,"E121.MirrorCS"),sQuery(id+"F0.wireOp",EDGE,"E122.MirrorCS"),sQuery(id+"F0.wireOp",EDGE,"E123.MirrorCS"),sQuery(id+"F0.wireOp",EDGE,"E124.MirrorCS"),sQuery(id+"F0.wireOp",EDGE,"E125.MirrorCS"),sQuery(id+"F0.wireOp",EDGE,"E126.MirrorCS"),sQuery(id+"F0.wireOp",EDGE,"E127.MirrorCS"),sQuery(id+"F0.wireOp",EDGE,"E128.MirrorCS"),sQuery(id+"F0.wireOp",EDGE,"E129.MirrorCS"),sQuery(id+"F0.wireOp",EDGE,"E130.MirrorCS"),sQuery(id+"F0.wireOp",EDGE,"E131.MirrorCS"),sQuery(id+"F0.wireOp",EDGE,"E132.MirrorCS"),sQuery(id+"F0.wireOp",EDGE,"E133.MirrorCS"),sQuery(id+"F0.wireOp",EDGE,"E134.MirrorCS"),sQuery(id+"F0.wireOp",EDGE,"E135.MirrorCS"),sQuery(id+"F0.wireOp",EDGE,"E137.MirrorCS"),sQuery(id+"F0.wireOp",EDGE,"E138.MirrorCS"),sQuery(id+"F0.wireOp",EDGE,"E139.MirrorCS"),sQuery(id+"F0.wireOp",EDGE,"E140.MirrorCS"),sQuery(id+"F0.wireOp",EDGE,"E141.MirrorCS"),sQuery(id+"F0.wireOp",EDGE,"E142.MirrorCS"),sQuery(id+"F0.wireOp",EDGE,"E143.MirrorCS"),sQuery(id+"F0.wireOp",EDGE,"E144.MirrorCS"),sQuery(id+"F0.wireOp",EDGE,"E145.MirrorCS"),sQuery(id+"F0.wireOp",EDGE,"E146.MirrorCS"),sQuery(id+"F0.wireOp",EDGE,"E148.MirrorCS"),sQuery(id+"F0.wireOp",EDGE,"E149.MirrorCS"),sQuery(id+"F0.wireOp",EDGE,"E150.MirrorCS"),sQuery(id+"F0.wireOp",EDGE,"E151.MirrorCS"),sQuery(id+"F0.wireOp",EDGE,"E152.MirrorCS"),sQuery(id+"F0.wireOp",EDGE,"E153.MirrorCS"),sQuery(id+"F0.wireOp",EDGE,"E154.MirrorCS"),sQuery(id+"F0.wireOp",EDGE,"E155.MirrorCS"),sQuery(id+"F0.wireOp",EDGE,"E156.MirrorCS"),sQuery(id+"F0.wireOp",EDGE,"E158.MirrorCS"),sQuery(id+"F0.wireOp",EDGE,"E159.MirrorCS"),sQuery(id+"F0.wireOp",EDGE,"E160.MirrorCS"),sQuery(id+"F0.wireOp",EDGE,"E161.MirrorCS"),sQuery(id+"F0.wireOp",EDGE,"E162.MirrorCS"),sQuery(id+"F0.wireOp",EDGE,"E163.MirrorCS"),sQuery(id+"F0.wireOp",EDGE,"E165.MirrorCS"),sQuery(id+"F0.wireOp",EDGE,"E166.MirrorCS"),sQuery(id+"F0.wireOp",EDGE,"E167.MirrorCS"),sQuery(id+"F0.wireOp",EDGE,"E168.MirrorCS"),sQuery(id+"F0.wireOp",EDGE,"E169.MirrorCS"),sQuery(id+"F0.wireOp",EDGE,"E170.MirrorCS"),sQuery(id+"F0.wireOp",EDGE,"E171.MirrorCS"),sQuery(id+"F0.wireOp",EDGE,"E172.MirrorCS"),sQuery(id+"F0.wireOp",EDGE,"E173.MirrorCS"),sQuery(id+"F0.wireOp",EDGE,"E174.MirrorCS"),sQuery(id+"F0.wireOp",EDGE,"E175.MirrorCS")])]});
            var Q1;
            Q1=qCreatedBy(makeId("Origin.pointOp"),VERTEX);
            transform(context, id + "F6", {"entities" : qUnion([Q0]), "transformType" : TransformType.SCALE_UNIFORMLY, "scale" : .71, "scalePoint" : qUnion([Q1]), "makeCopy" : false});
        }
    });
